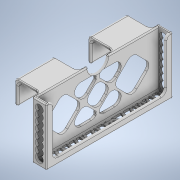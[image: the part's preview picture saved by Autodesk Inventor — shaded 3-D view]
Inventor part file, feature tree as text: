
AUTODESK INVENTOR PART (.ipt)
format: ipt  version: 2020 (Build 240168000, 168)  size: 1,085,952 bytes
history: native  units: in
note: dims shown in document units (in); Inventor stores cm internally (conversion verified against a paired STEP export)
features: fillet x11, extrude x10, sketch x10
ambient origin geometry x8: Origin, YZ Plane, XZ Plane, XY Plane, X Axis, Y Axis, Z Axis, Center Point
bodies: Solid1 (feature_tree)
feature tree (31):
  extrude  "Extrusion1"  Depth=6.1024in
  extrude  "Extrusion2"  Depth=0.1181in
  extrude  "Extrusion3"  Depth=0.1181in
  fillet  "Fillet1"  Radius=0.1181in
  extrude  "Extrusion4"  Depth=0.1181in
  extrude  "Extrusion5"  Depth=0.1181in
  extrude  "Extrusion6"  Depth=0.1181in
  extrude  "Extrusion7"  Depth=0.1181in
  extrude  "Extrusion8"  Depth=0.2362in
  fillet  "Fillet2"  Radius=0.2362in
  extrude  "Extrusion9"  Depth=0.1575in
  fillet  "Fillet3"  Radius=0.3937in
  fillet  "Fillet4"  Radius=0.2362in
  fillet  "Fillet5"  Radius=0.1575in
  fillet  "Fillet6"  Radius=0.1575in
  fillet  "Fillet7"  Radius=0.1575in
  fillet  "Fillet8"  Radius=0.1575in
  fillet  "Fillet9"  Radius=6.0236in
  extrude  "Extrusion10"  Depth=0.1575in
  fillet  "Fillet10"  Radius=0.1181in
  fillet  "Fillet11"  Radius=0.1181in
  sketch  "Sketch1"  dims[d0=0.4724in d1=6.1024in]
  sketch  "Sketch2"  dims[d2=0.1181in d3=0.1181in]
  sketch  "Sketch3"  dims[d4=0.1181in d5=0.1181in d6=0.1181in d7=0.0in]
  sketch  "Sketch4"  dims[d8=0.1181in d9=0.1181in]
  sketch  "Sketch5"  dims[d10=0.1181in d11=0.1181in]
  sketch  "Sketch6"  dims[d12=2.7559in d13=0.0in d14=0.1181in]
  sketch  "Sketch7"  dims[d15=0.1181in d16=0.1181in]
  sketch  "Sketch8"  dims[d17=0.1181in d18=0.2362in d19=0.2362in]
  sketch  "Sketch9"  dims[d20=0.2362in d21=0.2362in d22=0.3937in d23=0.0in d24=0.2362in d25=0.1575in d26=0.1575in d27=0.1575in d28=0.1575in d29=6.0236in]
  sketch  "Sketch11"  dims[d30=0.1181in d31=0.394in d32=0.1181in d33=0.1181in d34=0.0in d35=0.1575in d36=0.1575in d37=0.1575in d38=0.1575in d39=0.197in d40=3.1496in d42=0.309in d43=0.3937in d45=1.0in d47=6.6929in d48=0.0in d49=1.0in d50=0.1181in d51=0.0in d52=1.2598in d53=1.1811in d54=0.1575in d55=0.1575in d56=6.3386in d57=0.0in d58=0.3937in d59=0.3937in d60=0.3937in d61=0.3937in d62=1.2598in d63=0.0in d64=0.1575in d65=0.4724in d66=0.4724in d67=0.4724in d68=0.4724in d69=5.3937in d70=1.9291in d71=0.9645in d72=0.9645in d73=0.1181in d74=0.1181in d75=0.0591in d76=0.0591in d77=0.0591in d78=0.0591in d79=0.1181in d80=0.0in d81=0.315in d82=0.0394in d83=0.1969in d84=0.0591in d85=0.1575in d86=0.0787in d87=0.0394in d88=6.1024in d89=0.0in d90=0.1063in d91=0.1575in]
